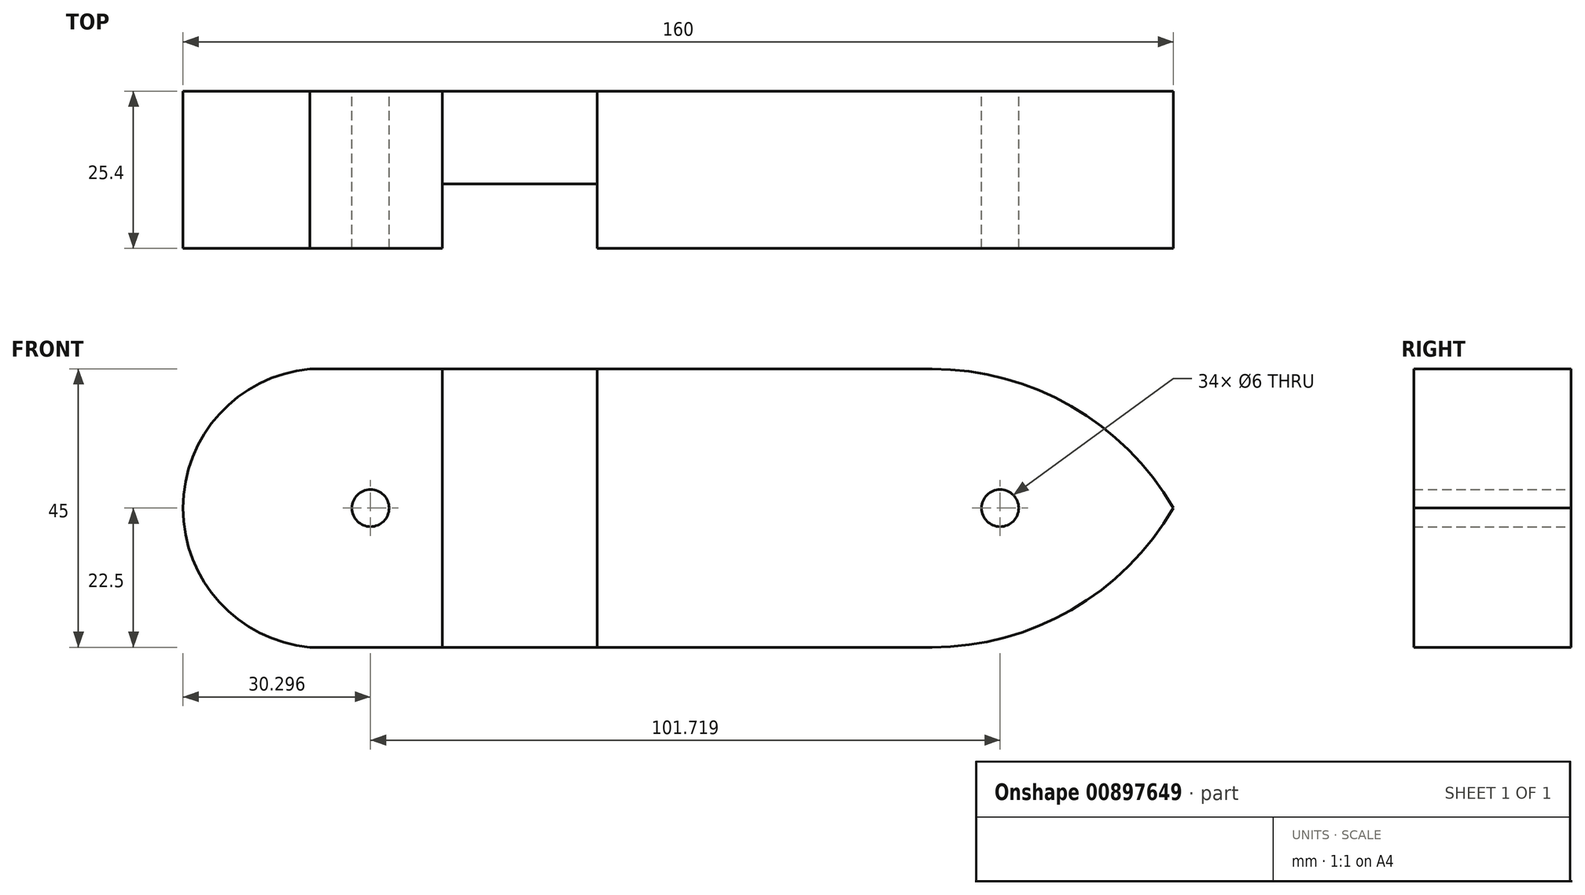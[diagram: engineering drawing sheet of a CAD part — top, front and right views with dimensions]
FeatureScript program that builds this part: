
annotation { "Feature Type Name" : "Feature", "Feature Type Description" : "" }
export const myFeature = defineFeature(function(context is Context, id is Id, definition is map)
    precondition{}
    {
        {
            var Q0;
            Q0=qCreatedBy(makeId("Front.planeOp"),FACE);
            var sketch = newSketch(context, id + "F0", { "sketchPlane" : qUnion([Q0])});
            skLineSegment(sketch, "E0.bottom", {"start": v(50.27, 22.5) * mm, "end": v(-50.27, 22.5) * mm});
            skLineSegment(sketch, "E0.top", {"start": v(50.27, -22.5) * mm, "end": v(-50.27, -22.5) * mm});
            skLineSegment(sketch, "E0.left", {"start": v(50.27, 22.5) * mm, "end": v(50.27, -22.5) * mm});
            skLineSegment(sketch, "E0.right", {"start": v(-50.27, 22.5) * mm, "end": v(-50.27, -22.5) * mm});
            skPoint(sketch, "E0.middle", {"position": v(0, 0) * mm});
            skArc(sketch, "E1", {"start": v(50.27, -22.5) * mm, "mid": v(72.77, -16.47) * mm, "end": v(89.24, 0) * mm});
            skArc(sketch, "E2", {"start": v(50.27, 22.5) * mm, "mid": v(72.77, 16.47) * mm, "end": v(89.24, 0) * mm});
            skArc(sketch, "E3", {"start": v(-50.27, 22.5) * mm, "mid": v(-70.76, 0) * mm, "end": v(-50.27, -22.5) * mm});
            skLineSegment(sketch, "E4", {"start": v(-28.85, 22.5) * mm, "end": v(-28.85, -22.5) * mm});
            skLineSegment(sketch, "E5", {"start": v(-3.85, 22.5) * mm, "end": v(-3.85, -22.5) * mm});
            skCircle(sketch, "E6", {"center": v(-40.46, 0) * mm, "radius": 3 * mm});
            skCircle(sketch, "E7", {"center": v(61.26, 0) * mm, "radius": 3 * mm});
            skPoint(sketch, "E7.centerSnap0", {"position": v(50.27, 0) * mm});
            skSolve(sketch);
        }
        {
            var Q0;
            Q0=makeQuery(id+"F0.imprint","IMPRINT",FACE,{"disambiguationData":[TD([[makeQuery(id+"F0.imprint","IMPRINT",EDGE,{"derivedFrom":sQuery(id+"F0.wireOp",EDGE,"E0.left")}),1.0]])]});
            var Q1;
            {var subQ0=sQuery(id+"F0.wireOp",EDGE,"E0.left");Q1=makeQuery(id+"F0.imprint","IMPRINT",FACE,{"disambiguationData":[TD([[makeQuery(id+"F0.imprint","IMPRINT",EDGE,{"derivedFrom":subQ0}),-1.0]])]});}
            var Q2;
            {var subQ2=sQuery(id+"F0.wireOp",EDGE,"E0.right");Q2=makeQuery(id+"F0.imprint","IMPRINT",FACE,{"disambiguationData":[TD([[makeQuery(id+"F0.imprint","IMPRINT",EDGE,{"derivedFrom":subQ2}),1.0]])]});}
            var Q3;
            Q3=makeQuery(id+"F0.imprint","IMPRINT",FACE,{"disambiguationData":[TD([[makeQuery(id+"F0.imprint","IMPRINT",EDGE,{"derivedFrom":sQuery(id+"F0.wireOp",EDGE,"E0.right")}),-1.0]])]});
            extrude(context, id + "F1", {"entities" : qUnion([Q0, Q1, Q2, Q3]), "depth" : 25.4 * mm, "offsetDistance" : 25.4 * mm});
        }
        {
            var Q0;
            {var subQ0=sQuery(id+"F0.wireOp",EDGE,"E4");Q0=makeQuery(id+"F0.imprint","IMPRINT",FACE,{"disambiguationData":[TD([[makeQuery(id+"F0.imprint","IMPRINT",EDGE,{"derivedFrom":subQ0}),1.0]])]});}
            extrude(context, id + "F2", {"entities" : qUnion([Q0]), "depth" : 15 * mm, "offsetDistance" : 25.4 * mm});
        }
    });
